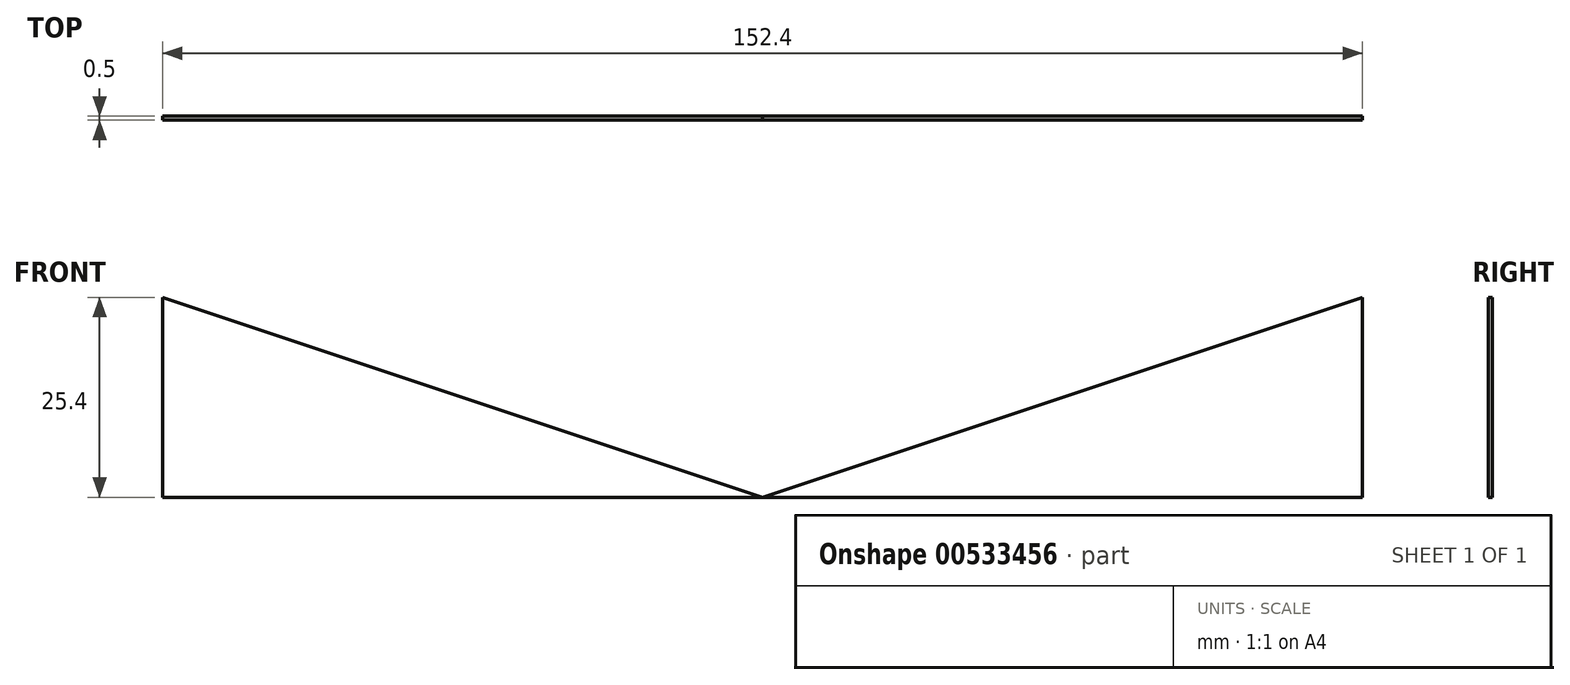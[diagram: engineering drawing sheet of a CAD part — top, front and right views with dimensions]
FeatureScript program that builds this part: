
annotation { "Feature Type Name" : "Feature", "Feature Type Description" : "" }
export const myFeature = defineFeature(function(context is Context, id is Id, definition is map)
    precondition{}
    {
        {
            var Q0;
            Q0=qCreatedBy(makeId("Front.planeOp"),FACE);
            var sketch = newSketch(context, id + "F0", { "sketchPlane" : qUnion([Q0])});
            skLineSegment(sketch, "E0", {"start": v(0, 0) * mm, "end": v(-76.2, 0) * mm});
            skLineSegment(sketch, "E1", {"start": v(-76.2, 0) * mm, "end": v(-76.2, 25.4) * mm});
            skLineSegment(sketch, "E2", {"start": v(-76.2, 25.4) * mm, "end": v(0, 0) * mm});
            skLineSegment(sketch, "E3", {"start": v(0, 0) * mm, "end": v(76.2, 0) * mm});
            skLineSegment(sketch, "E4", {"start": v(76.2, 0) * mm, "end": v(76.2, 25.4) * mm});
            skLineSegment(sketch, "E5", {"start": v(76.2, 25.4) * mm, "end": v(0, 0) * mm});
            skSolve(sketch);
        }
        {
            var Q0;
            Q0=makeQuery(id+"F0.imprint","IMPRINT",FACE,{"disambiguationData":[TD([[makeQuery(id+"F0.imprint","IMPRINT",EDGE,{"derivedFrom":sQuery(id+"F0.wireOp",EDGE,"E3")}),1.0]])]});
            var Q1;
            Q1=makeQuery(id+"F0.imprint","IMPRINT",FACE,{"disambiguationData":[TD([[makeQuery(id+"F0.imprint","IMPRINT",EDGE,{"derivedFrom":sQuery(id+"F0.wireOp",EDGE,"E0")}),-1.0]])]});
            extrude(context, id + "F1", {"entities" : qUnion([Q0, Q1]), "depth" : .5 * mm, "offsetDistance" : 25.4 * mm});
        }
    });
